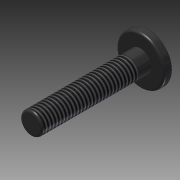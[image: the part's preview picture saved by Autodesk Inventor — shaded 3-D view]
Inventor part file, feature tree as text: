
AUTODESK INVENTOR PART (.ipt)
format: ipt  version: 2014 SP1 (Build 180222100, 222)  size: 123,392 bytes
history: native  units: in
note: dims shown in document units (in); Inventor stores cm internally (conversion verified against a paired STEP export)
features: sketch x2, revolve x1, fillet x1, extrude x1, thread x1
ambient origin geometry x8: Origin, YZ Plane, XZ Plane, XY Plane, X Axis, Y Axis, Z Axis, Center Point
bodies: Solid1 (feature_tree)
feature tree (6):
  revolve  "Revolution1"  [1 undecoded]
  fillet  "Fillet1"  Radius=0.2165in
  extrude  "Extrusion1"  TaperAngle=90.0deg  [1 undecoded]
  thread  "Thread1"  [1 undecoded]
  sketch  "Sketch1"  dims[d0=0.9843in d1=0.0787in d2=0.2165in]
  sketch  "Sketch2"  dims[d3=0.0984in d4=90.0deg d5=0.0197in d6=0.1181in d7=0.1181in d8=0.0in d9=1.1811in d10=0.1181in]
note: 3 required parameter values undecoded (feature->parameter linkage not recoverable at this tier; creation-order binding heuristic only, values carry confidence <= 0.55)